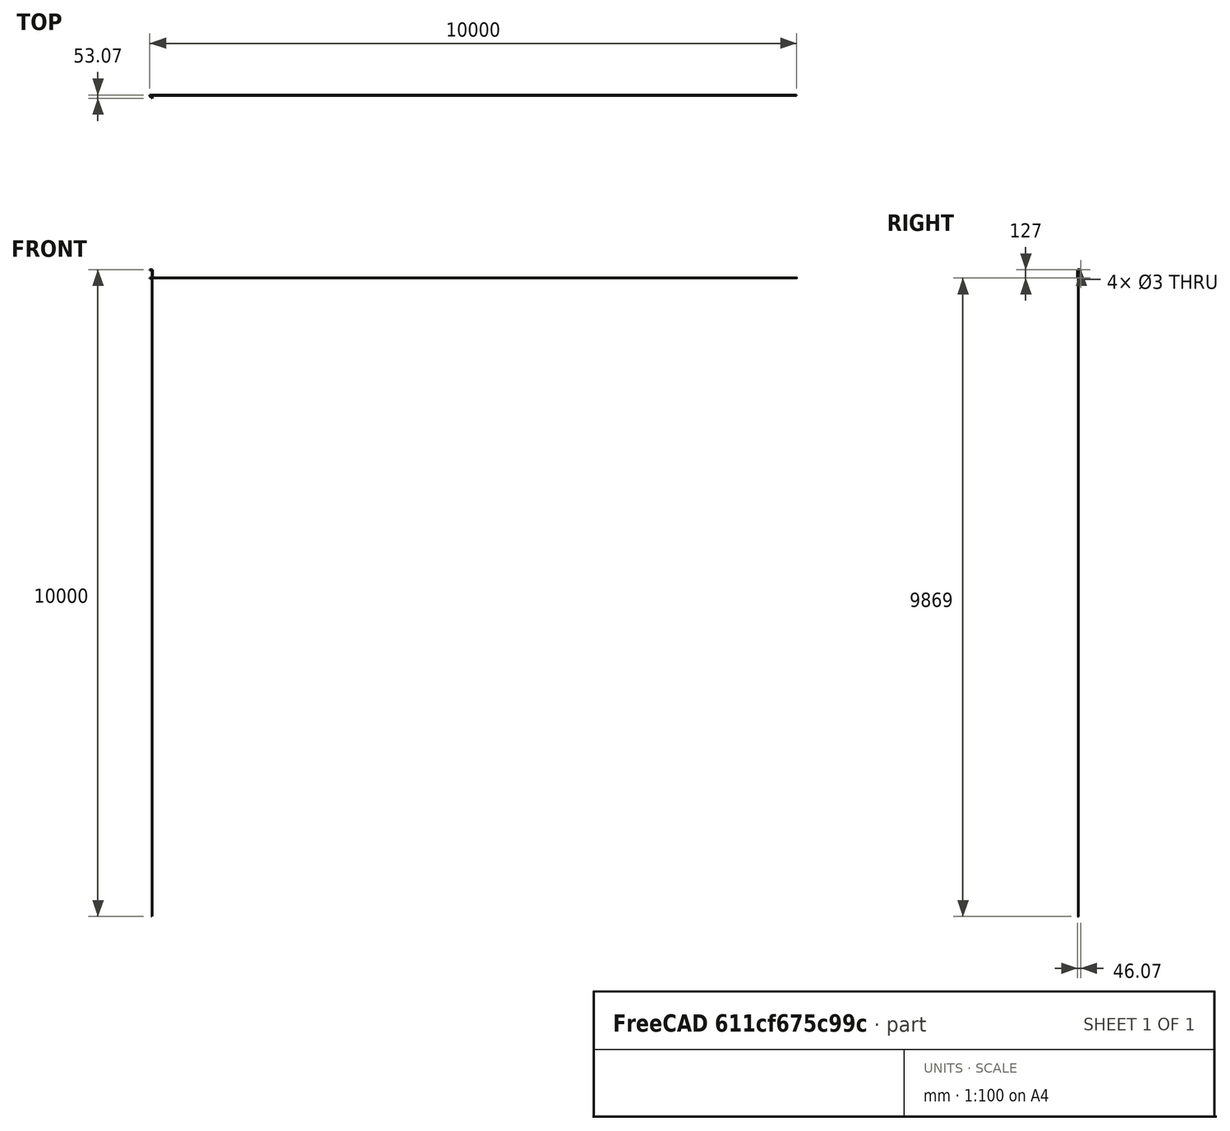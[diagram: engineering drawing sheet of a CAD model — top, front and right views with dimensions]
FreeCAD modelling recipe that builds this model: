
FCSTD DOCUMENT  (FreeCAD 0.16R6712 (Git))
Label: Guignol_Moteurs_Avant
License: All rights reserved
LicenseURL: http://en.wikipedia.org/wiki/All_rights_reserved
objects: Sketcher::SketchObject×6, PartDesign::Pad×3, PartDesign::Pocket×3, Mesh::Feature×2, Part::MultiFuse×1
note: 19 computed .brp shape members not serialized (recipe doc carries the construction recipe); baked Part::Feature solids carry a one-line shape summary decoded from their .brp

FEATURE [Sketcher::SketchObject] Sketch
  sketch-geometry (11):
    g0: LineSegment StartX=0 StartY=0 StartZ=0 EndX=0 EndY=10 EndZ=0
    g1: LineSegment StartX=0 StartY=0 StartZ=0 EndX=6.5 EndY=0 EndZ=0
    g2: LineSegment StartX=6.5 StartY=0 StartZ=0 EndX=6.5 EndY=10 EndZ=0
    g3: LineSegment StartX=-4 StartY=-4 StartZ=0 EndX=35.0698 EndY=-43.0698 EndZ=0
    g4: LineSegment StartX=-4 StartY=-4 StartZ=0 EndX=-4 EndY=10 EndZ=0
    g5: LineSegment StartX=-4 StartY=10 StartZ=0 EndX=0 EndY=10 EndZ=0
    g6: LineSegment StartX=6.5 StartY=10 StartZ=0 EndX=10.5 EndY=10 EndZ=0
    g7: LineSegment StartX=10.5 StartY=10 StartZ=0 EndX=10.5 EndY=-4 EndZ=0
    g8: LineSegment StartX=35.0698 StartY=-43.0698 StartZ=0 EndX=38.6053 EndY=-39.5343 EndZ=0
    g9: LineSegment StartX=38.6053 StartY=-39.5343 StartZ=0 EndX=6.78553 EndY=-7.71447 EndZ=0
    g10: LineSegment StartX=10.5 StartY=-4 StartZ=0 EndX=6.78553 EndY=-7.71447 EndZ=0
  constraints (32):
    c: Coincident(g0,g-1)
    c: Coincident(g1,g-1)
    c: Coincident(g1,g2)
    c: DistanceX(g4,g-1) = 4
    c: Distance(g2) = 10
    c: Distance(g0) = 10
    c: Distance(g1) = 6.5
    c: Angle(g2,g1) = 1.5708
    c: Coincident(g5,g4)
    c: Coincident(g5,g0)
    c: Angle(g5,g0) = 1.5708
    c: Distance(g5) = 4
    c: Coincident(g3,g4)
    c: Coincident(g6,g2)
    c: Coincident(g7,g6)
    c: Angle(g3,g1) = 0.785398
    c: Distance(g6) = 4
    c: Horizontal(g1)
    c: Horizontal(g6)
    c: Vertical(g4)
    c: Vertical(g7)
    c: Coincident(g8,g3)
    c: Coincident(g9,g8)
    c: Parallel(g9,g3)
    c: Angle(g8,g3) = 1.5708
    c: Distance(g8) = 5
    c: DistanceY(g3,g-1) = 4
    c: Coincident(g10,g7)
    c: Coincident(g9,g10)
    c: Angle(g9,g10) = 1.5708
    c: DistanceY(g7,g1) = 4
    c: Distance(g9) = 45
FEATURE [PartDesign::Pad] Pad
  Length = 7
  Length2 = 100
  Sketch = -> Sketch
  Type = 0
FEATURE [Sketcher::SketchObject] Sketch001
  ExternalGeometry = -> [Pad]
  Placement = pos=(-4,0,0) rot=(0.57735,-0.57735,-0.57735;2.0944rad)
  Support = -> Pad [Face5]
  sketch-geometry (1):
    g0: Circle CenterX=-3 CenterY=4 CenterZ=0 NormalX=0 NormalY=0 NormalZ=1 Radius=1.5
  constraints (3):
    c: DistanceX(g0,g-1) = 3
    c: Radius(g0) = 1.5
    c: DistanceY(g0,g-3) = 3
FEATURE [PartDesign::Pocket] Pocket
  Length = 5
  Sketch = -> Sketch001
  Type = 1
FEATURE [Sketcher::SketchObject] Sketch002
  Placement = pos=(0,0,128) rot=(0,0,1;0rad)
  sketch-geometry (11):
    g0: LineSegment StartX=0 StartY=0 StartZ=0 EndX=0 EndY=10 EndZ=0
    g1: LineSegment StartX=0 StartY=0 StartZ=0 EndX=6.5 EndY=0 EndZ=0
    g2: LineSegment StartX=6.5 StartY=0 StartZ=0 EndX=6.5 EndY=10 EndZ=0
    g3: LineSegment StartX=-4 StartY=-4 StartZ=0 EndX=35.0698 EndY=-43.0698 EndZ=0
    g4: LineSegment StartX=-4 StartY=-4 StartZ=0 EndX=-4 EndY=10 EndZ=0
    g5: LineSegment StartX=-4 StartY=10 StartZ=0 EndX=0 EndY=10 EndZ=0
    g6: LineSegment StartX=6.5 StartY=10 StartZ=0 EndX=10.5 EndY=10 EndZ=0
    g7: LineSegment StartX=10.5 StartY=10 StartZ=0 EndX=10.5 EndY=-4 EndZ=0
    g8: LineSegment StartX=35.0698 StartY=-43.0698 StartZ=0 EndX=38.6053 EndY=-39.5343 EndZ=0
    g9: LineSegment StartX=38.6053 StartY=-39.5343 StartZ=0 EndX=6.78553 EndY=-7.71447 EndZ=0
    g10: LineSegment StartX=10.5 StartY=-4 StartZ=0 EndX=6.78553 EndY=-7.71447 EndZ=0
  constraints (32):
    c: Coincident(g0,g-1)
    c: Coincident(g1,g-1)
    c: Coincident(g1,g2)
    c: DistanceX(g4,g-1) = 4
    c: Distance(g2) = 10
    c: Distance(g0) = 10
    c: Distance(g1) = 6.5
    c: Angle(g2,g1) = 1.5708
    c: Coincident(g5,g4)
    c: Coincident(g5,g0)
    c: Angle(g5,g0) = 1.5708
    c: Distance(g5) = 4
    c: Coincident(g3,g4)
    c: Coincident(g6,g2)
    c: Coincident(g7,g6)
    c: Angle(g3,g1) = 0.785398
    c: Distance(g6) = 4
    c: Horizontal(g1)
    c: Horizontal(g6)
    c: Vertical(g4)
    c: Vertical(g7)
    c: Coincident(g8,g3)
    c: Coincident(g9,g8)
    c: Parallel(g9,g3)
    c: Angle(g8,g3) = 1.5708
    c: Distance(g8) = 5
    c: DistanceY(g3,g-1) = 4
    c: Coincident(g10,g7)
    c: Coincident(g9,g10)
    c: Angle(g9,g10) = 1.5708
    c: DistanceY(g7,g1) = 4
    c: Distance(g9) = 45
FEATURE [PartDesign::Pad] Pad001
  Length = 7
  Length2 = 100
  Placement = pos=(0,0,128) rot=(0,0,1;0rad)
  Sketch = -> Sketch002
  Type = 0
FEATURE [Sketcher::SketchObject] Sketch003
  ExternalGeometry = -> [Pad001]
  Placement = pos=(-4,0,128) rot=(0.57735,-0.57735,-0.57735;2.0944rad)
  Support = -> Pad001 [Face5]
  sketch-geometry (1):
    g0: Circle CenterX=-3 CenterY=3 CenterZ=0 NormalX=0 NormalY=0 NormalZ=1 Radius=1.5
  constraints (3):
    c: DistanceX(g0,g-1) = 3
    c: Radius(g0) = 1.5
    c: DistanceY(g0,g-3) = 4
FEATURE [PartDesign::Pocket] Pocket001
  Length = 5
  Placement = pos=(0,0,128) rot=(0,0,1;0rad)
  Sketch = -> Sketch003
  Type = 1
FEATURE [Sketcher::SketchObject] Sketch004
  ExternalGeometry = -> [Pocket]
  Placement = pos=(0,0,0) rot=(1,0,0;3.14159rad)
  Support = -> Pocket [Face3]
  sketch-geometry (4):
    g0: LineSegment StartX=35.0698 StartY=43.0698 StartZ=0 EndX=38.6053 EndY=39.5343 EndZ=0
    g1: LineSegment StartX=38.6053 StartY=39.5343 StartZ=0 EndX=35.0698 EndY=35.9987 EndZ=0
    g2: LineSegment StartX=35.0698 StartY=35.9987 StartZ=0 EndX=31.5343 EndY=39.5343 EndZ=0
    g3: LineSegment StartX=31.5343 StartY=39.5343 StartZ=0 EndX=35.0698 EndY=43.0698 EndZ=0
  constraints (10):
    c: Coincident(g1,g0)
    c: Coincident(g2,g1)
    c: Coincident(g3,g2)
    c: Coincident(g0,g-5)
    c: PointOnObject(g1,g-5)
    c: PointOnObject(g2,g-4)
    c: Coincident(g0,g-4)
    c: Coincident(g0,g3)
    c: Distance(g0,g1) = 5
    c: Distance(g2,g0) = 5
FEATURE [PartDesign::Pad] Pad002
  Length = 128
  Length2 = 100
  Reversed = true
  Sketch = -> Sketch004
  Type = 0
FEATURE [Part::MultiFuse] Fusion
  Shapes = -> [Pocket001,Pad002]
FEATURE [Sketcher::SketchObject] Sketch005
  ExternalGeometry = -> [Fusion]
  Placement = pos=(0,0,135) rot=(0,0,1;0rad)
  Support = -> Fusion [Face4]
  sketch-geometry (2):
    g0: Circle CenterX=29.7665 CenterY=-34.231 CenterZ=0 NormalX=0 NormalY=0 NormalZ=1 Radius=0.75
    g1: LineSegment [constr] StartX=36.8376 StartY=-41.302 StartZ=0 EndX=29.7665 EndY=-34.231 EndZ=0
  constraints (5):
    c: PointOnObject(g1,g-4)
    c: Coincident(g1,g0)
    c: Symmetric(g-4,g-4,g1)
    c: Radius(g0) = 0.75
    c: Distance(g1) = 10
FEATURE [PartDesign::Pocket] Pocket002
  Length = 5
  Sketch = -> Sketch005
  Type = 1
FEATURE [Mesh::Feature] Bras_moteur
  Placement = pos=(3.5,3,-63) rot=(0.57735,-0.57735,-0.57735;4.18879rad)
FEATURE [Mesh::Feature] Bras_moteur001
  Placement = pos=(3.5,3,198) rot=(0.57735,0.57735,0.57735;4.18879rad)
